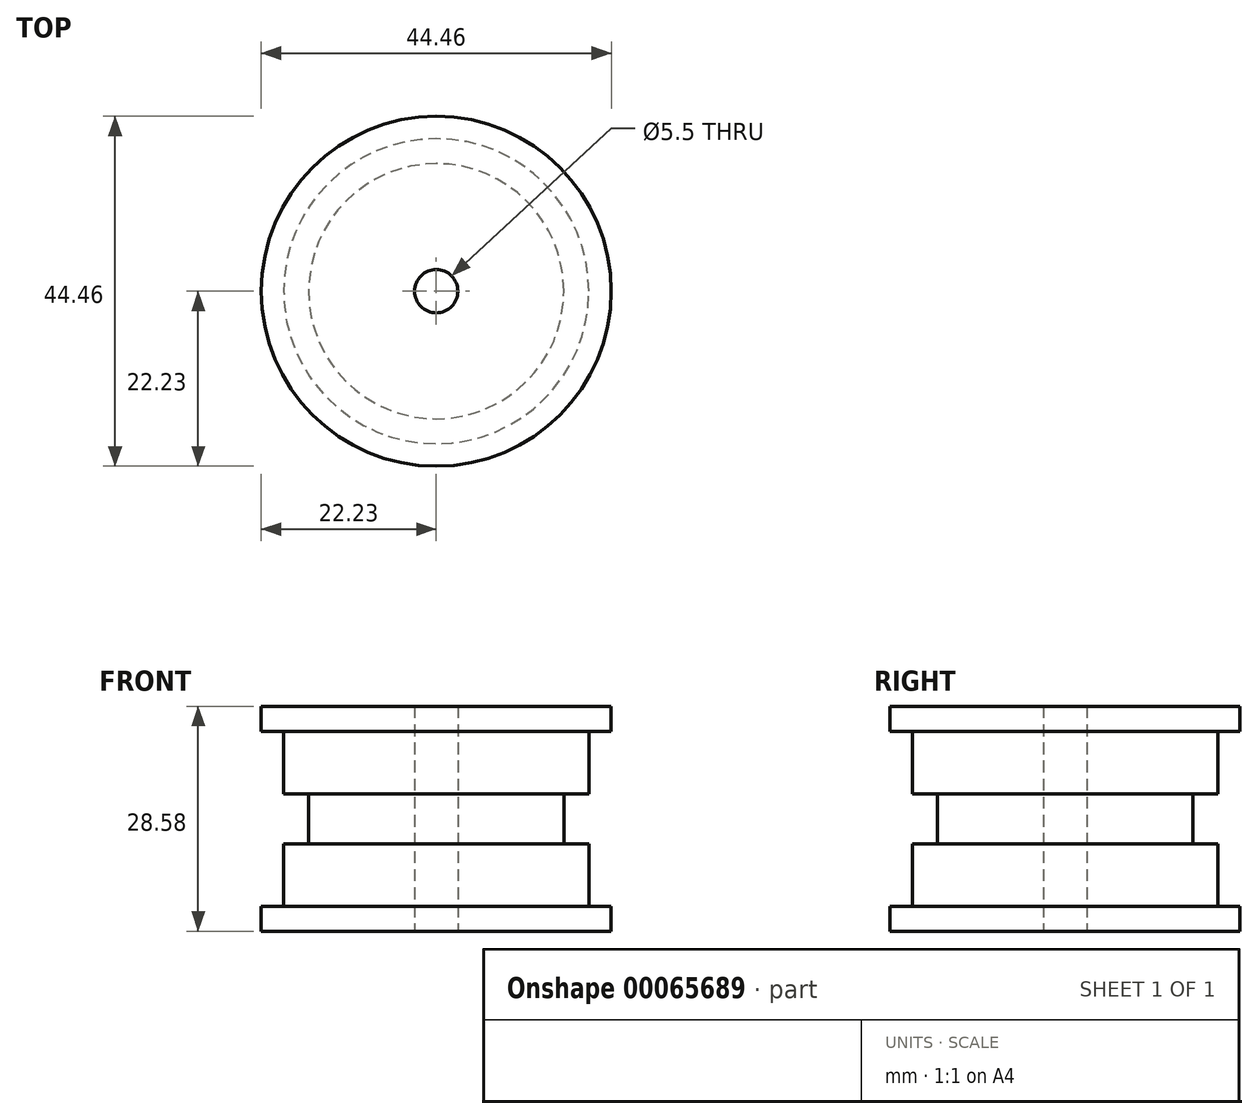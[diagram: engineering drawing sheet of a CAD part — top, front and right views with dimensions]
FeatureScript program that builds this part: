
annotation { "Feature Type Name" : "Feature", "Feature Type Description" : "" }
export const myFeature = defineFeature(function(context is Context, id is Id, definition is map)
    precondition{}
    {
        {
            var Q0;
            Q0=qCreatedBy(makeId("Right.planeOp"),FACE);
            var sketch = newSketch(context, id + "F0", { "sketchPlane" : qUnion([Q0])});
            skLineSegment(sketch, "E0", {"start": v(0, 0) * mm, "end": v(-22.23, 0) * mm});
            skLineSegment(sketch, "E1", {"start": v(-22.23, 0) * mm, "end": v(-22.23, -3.18) * mm});
            skLineSegment(sketch, "E2", {"start": v(-22.23, -3.17) * mm, "end": v(-19.38, -3.17) * mm});
            skLineSegment(sketch, "E3", {"start": v(-19.38, -25.4) * mm, "end": v(-22.22, -25.4) * mm});
            skLineSegment(sketch, "E4", {"start": v(-22.23, -25.4) * mm, "end": v(-22.23, -28.58) * mm});
            skLineSegment(sketch, "E5", {"start": v(-22.22, -28.58) * mm, "end": v(0, -28.58) * mm});
            skLineSegment(sketch, "E6", {"start": v(0, -28.58) * mm, "end": v(0, 0) * mm});
            skLineSegment(sketch, "E7", {"start": v(-19.38, -3.17) * mm, "end": v(-19.38, -11.11) * mm});
            skLineSegment(sketch, "E8", {"start": v(-19.38, -11.11) * mm, "end": v(-16.2, -11.11) * mm});
            skLineSegment(sketch, "E9", {"start": v(-16.2, -11.11) * mm, "end": v(-16.2, -17.46) * mm});
            skLineSegment(sketch, "E10", {"start": v(-16.2, -17.46) * mm, "end": v(-19.38, -17.46) * mm});
            skLineSegment(sketch, "E11", {"start": v(-19.38, -17.46) * mm, "end": v(-19.38, -25.4) * mm});
            skSolve(sketch);
        }
        {
            var Q0;
            Q0=makeQuery(id+"F0.imprint","IMPRINT",FACE,{"disambiguationData":[TD([[makeQuery(id+"F0.imprint","IMPRINT",EDGE,{"derivedFrom":sQuery(id+"F0.wireOp",EDGE,"E0")}),1.0]])]});
            var Q1;
            Q1=sQuery(id+"F0.wireOp",EDGE,"E6");
            revolve(context, id + "F1", {"entities" : qUnion([Q0]), "axis" : qUnion([Q1]), "revolveType" : RevolveType.FULL});
        }
        {
            var Q0;
            Q0=makeQuery(id+"F1.opRevolve","SWEPT_FACE",FACE,{"disambiguationData":[OSD([sQuery(id+"F0.wireOp",EDGE,"E5")])]});
            var sketch = newSketch(context, id + "F2", { "sketchPlane" : qUnion([Q0])});
            skCircle(sketch, "E12", {"center": v(0, 0) * mm, "radius": 2.75 * mm});
            skSolve(sketch);
        }
        {
            var Q0;
            Q0=sQuery(id+"F2.wireOp",VERTEX,"E12.center");
            var Q1;
            Q1=makeQuery(id+"F1.opRevolve","SWEPT_BODY",BODY,{"disambiguationData":[OSD([sQuery(id+"F0.wireOp",EDGE,"E0"),sQuery(id+"F0.wireOp",EDGE,"E1"),sQuery(id+"F0.wireOp",EDGE,"E2"),sQuery(id+"F0.wireOp",EDGE,"E3"),sQuery(id+"F0.wireOp",EDGE,"E4"),sQuery(id+"F0.wireOp",EDGE,"E5"),sQuery(id+"F0.wireOp",EDGE,"E6"),sQuery(id+"F0.wireOp",EDGE,"E7"),sQuery(id+"F0.wireOp",EDGE,"E8"),sQuery(id+"F0.wireOp",EDGE,"E9"),sQuery(id+"F0.wireOp",EDGE,"E10"),sQuery(id+"F0.wireOp",EDGE,"E11")])]});
            hole(context, id + "F3", {"style" : HoleStyle.SIMPLE, "holeDiameter" : 5.5 * mm, "endStyle" : HoleEndStyle.THROUGH, "locations" : qUnion([Q0]), "scope" : qUnion([Q1])});
        }
    });
